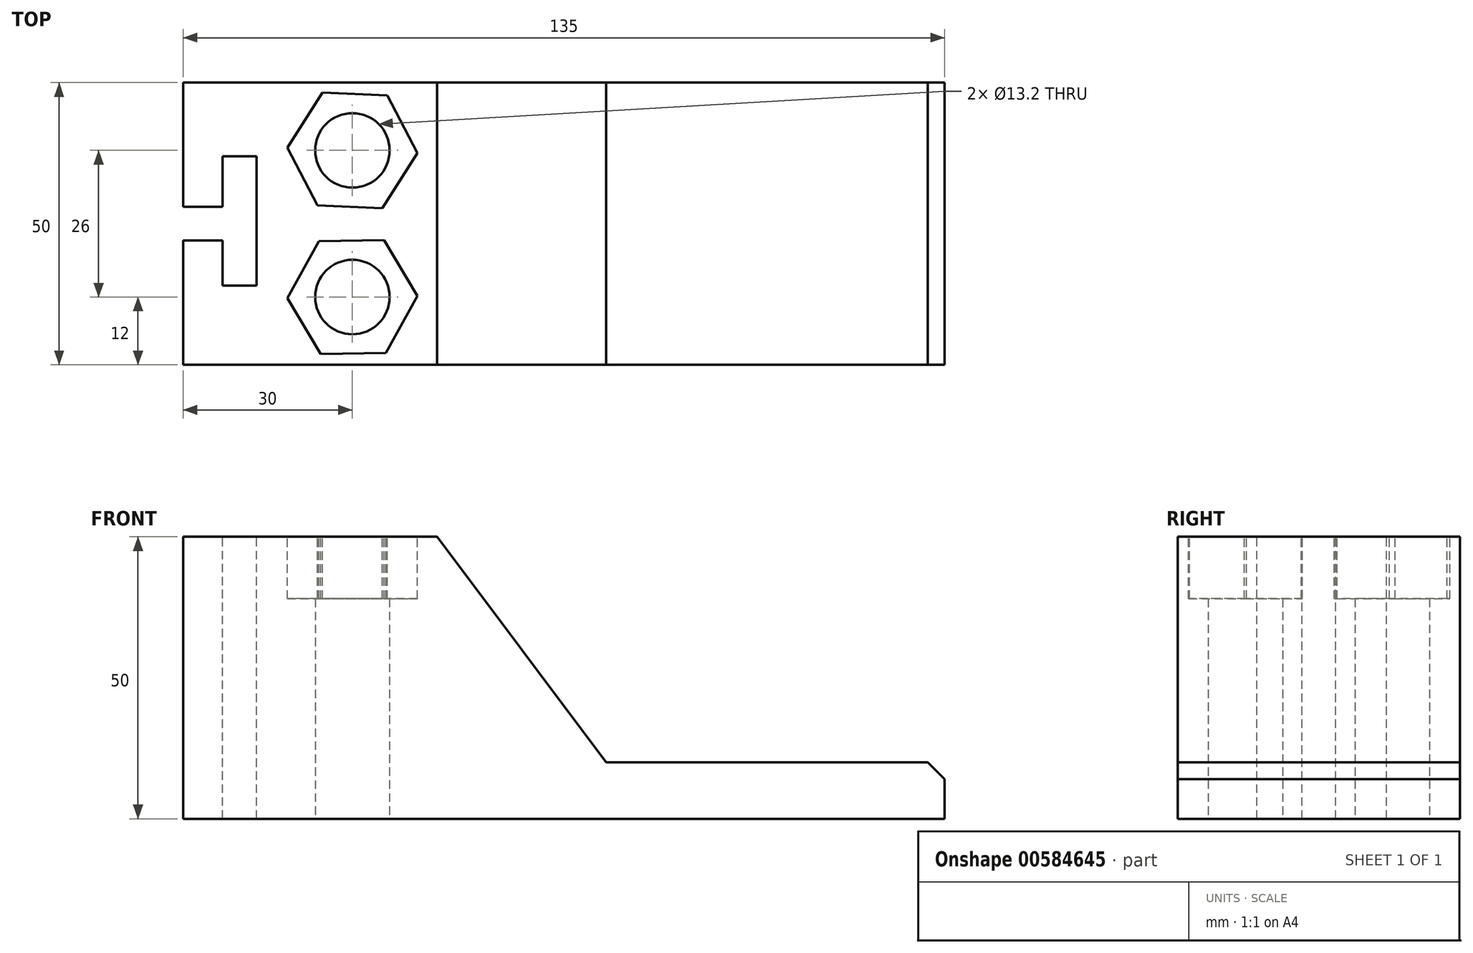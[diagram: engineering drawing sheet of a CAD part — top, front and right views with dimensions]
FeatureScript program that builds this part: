
annotation { "Feature Type Name" : "Feature", "Feature Type Description" : "" }
export const myFeature = defineFeature(function(context is Context, id is Id, definition is map)
    precondition{}
    {
        {
            var Q0;
            Q0=qCreatedBy(makeId("Front.planeOp"),FACE);
            var sketch = newSketch(context, id + "F0", { "sketchPlane" : qUnion([Q0])});
            skLineSegment(sketch, "E0.bottom", {"start": v(67.5, 5) * mm, "end": v(-67.5, 5) * mm});
            skLineSegment(sketch, "E0.top", {"start": v(67.5, -5) * mm, "end": v(-67.5, -5) * mm});
            skLineSegment(sketch, "E0.left", {"start": v(67.5, 5) * mm, "end": v(67.5, -5) * mm});
            skLineSegment(sketch, "E0.right", {"start": v(-67.5, 5) * mm, "end": v(-67.5, -5) * mm});
            skPoint(sketch, "E0.middle", {"position": v(0, 0) * mm});
            skLineSegment(sketch, "E1", {"start": v(-67.5, 5) * mm, "end": v(-67.5, 45) * mm});
            skLineSegment(sketch, "E2", {"start": v(-67.5, 45) * mm, "end": v(-22.5, 45) * mm});
            skLineSegment(sketch, "E3", {"start": v(-22.5, 45) * mm, "end": v(7.5, 5) * mm});
            skSolve(sketch);
        }
        {
            var Q0;
            Q0=makeQuery(id+"F0.imprint","IMPRINT",FACE,{"disambiguationData":[TD([[makeQuery(id+"F0.imprint","IMPRINT",EDGE,{"derivedFrom":sQuery(id+"F0.wireOp",EDGE,"E0.top")}),-1.0]])]});
            extrude(context, id + "F1", {"entities" : qUnion([Q0]), "endBound" : BoundingType.SYMMETRIC, "depth" : 50 * mm, "offsetDistance" : 25 * mm});
        }
        {
            var Q0;
            {var subQ0=sQuery(id+"F0.wireOp",EDGE,"E1");Q0=makeQuery(id+"F0.imprint","IMPRINT",FACE,{"disambiguationData":[TD([[makeQuery(id+"F0.imprint","IMPRINT",EDGE,{"derivedFrom":subQ0}),-1.0]])]});}
            var Q1;
            Q1 = qSketchRegion(id + "F3", true);
            extrude(context, id + "F2", {"entities" : qUnion([Q0, Q1]), "operationType" : NewBodyOperationType.ADD, "endBound" : BoundingType.SYMMETRIC, "depth" : 50 * mm, "offsetDistance" : 25 * mm});
        }
        {
            var Q0;
            Q0=makeQuery(id+"F1.opExtrude","SWEPT_FACE",FACE,{"disambiguationData":[OSD([sQuery(id+"F0.wireOp",EDGE,"E0.top")])]});
            var sketch = newSketch(context, id + "F3", { "sketchPlane" : qUnion([Q0])});
            skPoint(sketch, "E4", {"position": v(-37.5, 13) * mm});
            skPoint(sketch, "E5", {"position": v(-37.5, -13) * mm});
            skSolve(sketch);
        }
        {
            var Q0;
            Q0=sQuery(id+"F3.wireOp",VERTEX,"E4");
            var Q1;
            Q1=sQuery(id+"F3.wireOp",VERTEX,"E5");
            var Q2;
            Q2=makeQuery(id+"F1.opExtrude","SWEPT_BODY",BODY,{"disambiguationData":[OSD([sQuery(id+"F0.wireOp",EDGE,"E0.bottom"),sQuery(id+"F0.wireOp",EDGE,"E0.top"),sQuery(id+"F0.wireOp",EDGE,"E0.left"),sQuery(id+"F0.wireOp",EDGE,"E0.right")])]});
            hole(context, id + "F4", {"style" : HoleStyle.C_BORE, "endStyle" : HoleEndStyle.THROUGH, "holeDiameter" : 13.2 * mm, "cBoreDiameter" : 23 * mm, "cBoreDepth" : 0 * mm, "majorDiameter" : 5 * mm, "isTappedThrough" : true, "tappedDepth" : 12 * mm, "tapClearance" : 3, "startFromSketch" : true, "locations" : qUnion([Q0, Q1]), "scope" : qUnion([Q2])});
        }
        {
            var Q0;
            Q0=makeQuery(id+"F2.opExtrude","SWEPT_FACE",FACE,{"disambiguationData":[OSD([sQuery(id+"F0.wireOp",EDGE,"E2")])]});
            var sketch = newSketch(context, id + "F5", { "sketchPlane" : qUnion([Q0])});
            skLineSegment(sketch, "E6", {"start": v(-67.5, 3) * mm, "end": v(-60.5, 3) * mm});
            skLineSegment(sketch, "E7", {"start": v(-60.5, 3) * mm, "end": v(-60.5, 11.97) * mm});
            skLineSegment(sketch, "E8", {"start": v(-60.5, 11.97) * mm, "end": v(-54.5, 11.97) * mm});
            skLineSegment(sketch, "E9", {"start": v(-54.5, 11.97) * mm, "end": v(-54.5, -10.96) * mm});
            skLineSegment(sketch, "E10", {"start": v(-54.5, -10.96) * mm, "end": v(-60.5, -10.96) * mm});
            skLineSegment(sketch, "E11", {"start": v(-60.5, -10.96) * mm, "end": v(-60.5, -3) * mm});
            skLineSegment(sketch, "E12", {"start": v(-60.5, -3) * mm, "end": v(-67.5, -3) * mm});
            skLineSegment(sketch, "E13", {"start": v(-67.5, -3) * mm, "end": v(-67.5, 3) * mm});
            skSolve(sketch);
        }
        {
            var Q0;
            Q0 = qSketchRegion(id + "F5", true);
            extrude(context, id + "F6", {"entities" : qUnion([Q0]), "operationType" : NewBodyOperationType.REMOVE, "endBound" : BoundingType.THROUGH_ALL, "oppositeDirection" : true, "depth" : 25 * mm, "offsetDistance" : 25 * mm});
        }
        {
            var Q0;
            Q0=makeQuery(id+"F2.opExtrude","SWEPT_FACE",FACE,{"disambiguationData":[OSD([sQuery(id+"F0.wireOp",EDGE,"E2")])]});
            var sketch = newSketch(context, id + "F7", { "sketchPlane" : qUnion([Q0])});
            skCircle(sketch, "E14.cCircle", {"center": v(-37.5, -13) * mm, "radius": 10 * mm, "construction": true});
            skLineSegment(sketch, "E14.0", {"start": v(-31.9, -2.9) * mm, "end": v(-25.95, -12.8) * mm});
            skLineSegment(sketch, "E14.1", {"start": v(-25.95, -12.8) * mm, "end": v(-31.56, -22.9) * mm});
            skLineSegment(sketch, "E14.2", {"start": v(-31.56, -22.9) * mm, "end": v(-43.1, -23.1) * mm});
            skLineSegment(sketch, "E14.3", {"start": v(-43.1, -23.1) * mm, "end": v(-49.05, -13.2) * mm});
            skLineSegment(sketch, "E14.4", {"start": v(-49.05, -13.2) * mm, "end": v(-43.44, -3.1) * mm});
            skLineSegment(sketch, "E14.5", {"start": v(-43.44, -3.1) * mm, "end": v(-31.9, -2.9) * mm});
            skPoint(sketch, "E14.0.midPoint", {"position": v(-28.93, -7.85) * mm});
            skCircle(sketch, "E15.cCircle", {"center": v(-37.5, 13) * mm, "radius": 10 * mm, "construction": true});
            skLineSegment(sketch, "E15.0", {"start": v(-31.3, 22.74) * mm, "end": v(-25.96, 12.5) * mm});
            skLineSegment(sketch, "E15.1", {"start": v(-25.96, 12.5) * mm, "end": v(-32.17, 2.76) * mm});
            skLineSegment(sketch, "E15.2", {"start": v(-32.17, 2.76) * mm, "end": v(-43.7, 3.26) * mm});
            skLineSegment(sketch, "E15.3", {"start": v(-43.7, 3.26) * mm, "end": v(-49.04, 13.5) * mm});
            skLineSegment(sketch, "E15.4", {"start": v(-49.04, 13.5) * mm, "end": v(-42.83, 23.24) * mm});
            skLineSegment(sketch, "E15.5", {"start": v(-42.83, 23.24) * mm, "end": v(-31.3, 22.74) * mm});
            skPoint(sketch, "E15.0.midPoint", {"position": v(-28.63, 17.62) * mm});
            skSolve(sketch);
        }
        {
            var Q0;
            Q0 = qSketchRegion(id + "F7", true);
            extrude(context, id + "F8", {"entities" : qUnion([Q0]), "operationType" : NewBodyOperationType.REMOVE, "oppositeDirection" : true, "depth" : 11 * mm, "offsetDistance" : 25 * mm});
        }
        {
            var Q0;
            Q0=makeQuery(id+"F1.opExtrude","SWEPT_EDGE",EDGE,{"disambiguationData":[OSD([sQuery(id+"F0.wireOp",EDGE,"E0.bottom"),sQuery(id+"F0.wireOp",EDGE,"E0.left")])]});
            chamfer(context, id + "F9", {"entities" : qUnion([Q0]), "width" : 3 * mm, "tangentPropagation" : true});
        }
    });
